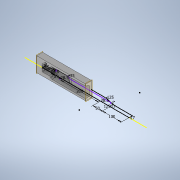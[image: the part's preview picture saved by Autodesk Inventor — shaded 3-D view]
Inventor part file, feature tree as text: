
AUTODESK INVENTOR PART (.ipt)
format: ipt  version: 2022 (Build 260153000, 153)  size: 235,520 bytes
history: native  units: mm
features: sketch x2, extrude x2, plane x2, revolve x1, fillet x1, boolean_combine x1, split x1
ambient origin geometry x8: Origin, YZ Plane, XZ Plane, XY Plane, X Axis, Y Axis, Z Axis, Center Point
bodies: Solid2 (feature_tree), Solid3 (feature_tree)
feature tree (10):
  sketch  "Sketch1"  dims[d0=41.0mm d1=6.0mm]
  revolve  "Revolution2"  [1 undecoded]
  extrude  "Extrusion2"  Depth=31.5mm
  fillet  "Fillet1"  Radius=50.0mm
  extrude  "Extrusion3"  Depth=31.5mm
  boolean_combine  "Combine1"
  plane  "Work Plane2"
  split  "Split1"
  sketch  "Sketch2"  dims[d2=59.0mm d3=200.0mm d4=50.0mm d5=100.0mm d6=19.5mm d7=19.5mm d8=28.5mm d10=28.5mm d11=17.0mm d12=17.0mm d13=2.0mm d14=8.0mm d16=125.0mm d17=125.0mm d18=2.0mm d25=35.0mm d26=28.5mm d27=180.0deg d28=100.0mm d29=0.0mm d30=2.0mm d31=516.0mm d32=77.0mm d33=31.5mm d34=0.0mm d35=-30.0mm d36=258.0mm d19=0.872665mm d20=0.872665mm]
  plane  "Work Plane1"
note: 1 required parameter value undecoded (feature->parameter linkage not recoverable at this tier; creation-order binding heuristic only, values carry confidence <= 0.55)
